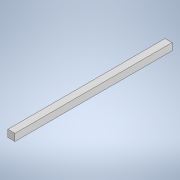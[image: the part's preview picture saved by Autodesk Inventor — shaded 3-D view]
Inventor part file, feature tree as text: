
AUTODESK INVENTOR PART (.ipt)
format: ipt  version: 2020 (Build 240168000, 168)  size: 95,232 bytes
history: native  units: mm
features: other x3, plane x1, extrude x1, sketch x1
ambient origin geometry x8: Origin, YZ Plane, XZ Plane, XY Plane, X Axis, Y Axis, Z Axis, Center Point
bodies: Solid1 (feature_tree)
feature tree (6):
  plane  "Work Plane1"
  extrude  "Extrusion1"  Depth=25.0mm
  sketch  "Sketch1"  dims[d0=25.0mm d1=25.0mm d2=556.0mm d3=0.0mm]
  parser-record x1  (decoder bookkeeping rows leaked as tree rows — omitted from the tree; the rows remain in map.json)
  other  "maquete.iam"
  other  "anteriorvertical:1"
note: 1 file-system path scrubbed to <path> (originals preserved in map.json)
